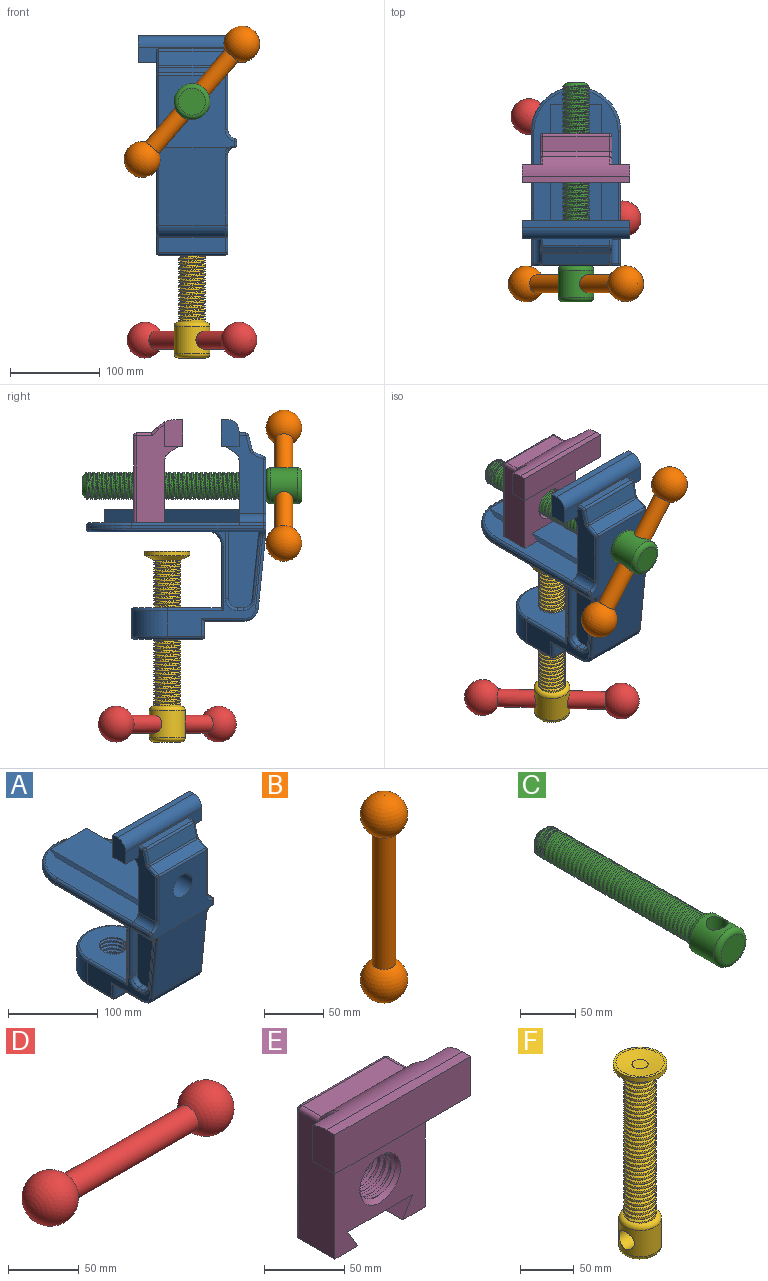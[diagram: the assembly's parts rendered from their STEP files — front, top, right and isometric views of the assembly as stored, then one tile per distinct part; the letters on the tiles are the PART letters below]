
ASSEMBLY  parts=6 mates=5
PART A: 123 faces, bbox 121.3x205.7x246.3 mm
  f0: cylinder r=15mm len=35mm, axis (0,0,1), area 1354.5mm2, adj f2,f4,f120,f121,f122
  f1: plane 117x106.29mm, normal (1,0,0), area 2063.5mm2, adj f8,f26,f77,f86,f87,f88,f89,f90
  f2: plane 98.33x75.33mm, normal (0,0,1), area 5812mm2, adj f0,f7,f103,f105,f107,f121,f122
  f3: plane 94.79x81.43mm, normal (0,-1,0), area 5458.1mm2, adj f27,f36,f57,f59,f60,f64,f65,f67
  f4: plane 75.45x74.02mm, normal (0,0,-1), area 4288.3mm2, adj f0,f90,f92,f93,f94
  f5: plane 74x44.99mm, normal (0,0,-1), area 3328.9mm2, adj f6,f84,f88,f97
  f6: plane 74x17mm, normal (0,-1,0), area 1258mm2, adj f5,f89,f93,f96
  f7: plane 74x70mm, normal (0,1,0), area 5180mm2, adj f2,f76,f102,f106
  f8: plane 193.33x95.05mm, normal (0,0,-1), area 12981.5mm2, adj f1,f25,f28,f29,f31,f32,f34,f35
  f9: plane 167x94mm, normal (0,0,1), area 8749.9mm2, adj f13,f21,f22,f23,f73,f74,f75
  f10: plane 147x4mm, normal (1,0,0), area 588mm2, adj f11,f65,f68,f75
  f11: cylinder r=50mm len=100mm, axis (0,0,-1), area 628.3mm2, adj f10,f12,f70,f74
  f12: plane 147x4mm, normal (-1,0,0), area 588mm2, adj f11,f71,f72,f73
  f13: plane 100x72.47mm, normal (0,1,0), area 4179.3mm2, adj f9,f14,f15,f16,f17,f22,f23,f24
  f14: plane 87x42mm, normal (-1,0,0), area 2053mm2, adj f13,f16,f37,f42,f43,f44,f47,f52
  f15: plane 87x42mm, normal (1,0,0), area 2053mm2, adj f13,f17,f37,f42,f43,f44,f45,f49
  f16: cylinder r=10mm len=27mm, axis (0,-1,0), area 361.2mm2, adj f13,f14,f66,f67
  f17: cylinder r=10mm len=27mm, axis (0,1,0), area 361.2mm2, adj f13,f15,f60,f61
  f18: plane 74x7.66mm, normal (0,0,1), area 566.7mm2, adj f42,f45,f47,f48
  f19: plane 74x12.11mm, normal (0,-0.45,0.89), area 1001.7mm2, adj f53,f54,f58,f59
  f20: plane 74x16.39mm, normal (0,-0.97,0.24), area 1250.1mm2, adj f48,f49,f52,f53
  f21: plane 57.32x15mm, normal (0,1,0), area 729.9mm2, adj f9,f22,f23,f24
  f22: plane 150x15mm, normal (-0.87,0,-0.5), area 2598.1mm2, adj f9,f13,f21,f24
  f23: plane 150x15mm, normal (0.87,0,-0.5), area 2598.1mm2, adj f9,f13,f21,f24
  f24: plane 150x57.32mm, normal (0,0,1), area 8598.1mm2, adj f13,f21,f22,f23
  f25: plane 117x106.29mm, normal (-1,0,0), area 2063.5mm2, adj f8,f26,f78,f94,f96,f97,f98,f99
  f26: cylinder r=40mm len=80mm, axis (0,0,1), area 3644.2mm2, adj f1,f25,f92,f105
  f27: plane 86.49x80.33mm, normal (0,-1,-0.1), area 6446.7mm2, adj f3,f84,f85,f86,f99,f100
  f28: plane 75x7mm, normal (0,-1,0), area 525mm2, adj f8,f31,f82,f114
  f29: plane 76x9.58mm, normal (0,1,0.1), area 540.1mm2, adj f8,f31,f79,f118,f119
  f30: plane 7x6.41mm, normal (0,0,1), area 44.9mm2, adj f31,f79,f82,f116
  f31: plane 85x33.96mm, normal (1,0,0), area 2487mm2, adj f8,f28,f29,f30,f79,f82
  f32: plane 75x7mm, normal (0,-1,0), area 525mm2, adj f8,f35,f81,f108
  f33: plane 7x6.41mm, normal (0,0,1), area 44.9mm2, adj f35,f80,f81,f110
  f34: plane 76x9.58mm, normal (0,1,0.1), area 540.1mm2, adj f8,f35,f80,f112,f113
  f35: plane 85x33.96mm, normal (-1,0,0), area 2487mm2, adj f8,f32,f33,f34,f80,f81
  f36: cylinder r=15mm len=30mm, axis (0,-1,0), area 2827.4mm2, adj f3,f13
  f37: plane 120x20mm, normal (0,0,-1), area 1200mm2, adj f14,f15,f38,f40,f41,f42,f43
  f38: plane 30x20mm, normal (-1,0,0), area 563.7mm2, adj f37,f39,f41,f42,f83
  f39: plane 120x7mm, normal (0,0,1), area 840mm2, adj f38,f40,f41,f83
  f40: plane 30x20mm, normal (1,0,0), area 563.7mm2, adj f37,f39,f41,f42,f83
  f41: plane 120x30mm, normal (0,1,0), area 3600mm2, adj f37,f38,f39,f40
  f42: plane 120x17mm, normal (0,-1,0), area 843.9mm2, adj f14,f15,f18,f37,f38,f40,f45,f47
  f43: plane 80x10.55mm, normal (0,0.55,-0.83), area 1014.1mm2, adj f14,f15,f37,f44
  f44: cylinder r=10mm len=80mm, axis (1,0,0), area 786.2mm2, adj f13,f14,f15,f43
  f45: cylinder r=3mm len=7.66mm, axis (0,-1,0), area 36.1mm2, adj f15,f18,f42,f46
  f46: sphere r=3mm, area 11.9mm2, adj f45,f48,f49
  f47: cylinder r=3mm len=7.66mm, axis (0,1,0), area 36.1mm2, adj f14,f18,f42,f50
  f48: cylinder r=3mm len=74mm, axis (1,0,0), area 294.3mm2, adj f18,f20,f46,f50
  f49: cylinder r=3mm len=17.12mm, axis (0,-0.24,-0.97), area 79.6mm2, adj f15,f20,f46,f51
  f50: sphere r=3mm, area 12.4mm2, adj f47,f48,f52
  f51: torus R=6mm, axis (1,0,0), area 16.6mm2, adj f15,f49,f53,f54
  f52: cylinder r=3mm len=17.12mm, axis (0,-0.24,-0.97), area 79.6mm2, adj f14,f20,f50,f55
  f53: cylinder r=3mm len=74mm, axis (1,0,0), area 191.4mm2, adj f19,f20,f51,f55
  f54: cylinder r=3mm len=13.45mm, axis (0,0.89,0.45), area 63.8mm2, adj f15,f19,f51,f56
  f55: torus R=6mm, axis (1,0,0), area 16.6mm2, adj f14,f52,f53,f58
  f56: sphere r=3mm, area 7.1mm2, adj f54,f57,f59
  f57: cylinder r=3mm len=60.65mm, axis (0,0,1), area 285.8mm2, adj f3,f15,f56,f60
  f58: cylinder r=3mm len=13.45mm, axis (0,0.89,0.45), area 63.8mm2, adj f14,f19,f55,f62
  f59: cylinder r=3mm len=74mm, axis (-1,0,0), area 245.8mm2, adj f3,f19,f56,f62
  f60: torus R=13mm, axis (0,1,0), area 69.9mm2, adj f3,f17,f57,f63
  f61: cylinder r=3mm len=27mm, axis (0,1,0), area 113.1mm2, adj f13,f17,f63,f75
  f62: sphere r=3mm, area 7.1mm2, adj f58,f59,f64
  f63: sphere r=3mm, area 12.1mm2, adj f60,f61,f65,f75
  f64: cylinder r=3mm len=60.65mm, axis (0,0,-1), area 285.8mm2, adj f3,f14,f62,f67
  f65: cylinder r=3mm len=6.71mm, axis (0,0,1), area 27.3mm2, adj f3,f10,f63,f68,f75,f85
  f66: cylinder r=3mm len=27mm, axis (0,-1,0), area 113.1mm2, adj f13,f16,f69,f73
  f67: torus R=13mm, axis (0,1,0), area 69.9mm2, adj f3,f16,f64,f69
  f68: cylinder r=3mm len=149.36mm, axis (0,1,0), area 698.6mm2, adj f8,f10,f65,f70,f77,f85
  f69: sphere r=3mm, area 12.1mm2, adj f66,f67,f71,f73
  f70: torus R=47mm, axis (0,0,1), area 724.1mm2, adj f8,f11,f68,f72
  f71: cylinder r=3mm len=6.71mm, axis (0,0,-1), area 27.3mm2, adj f3,f12,f69,f72,f73,f100
  f72: cylinder r=3mm len=149.36mm, axis (0,-1,0), area 698.6mm2, adj f8,f12,f70,f71,f78,f100
  f73: cylinder r=3mm len=147.35mm, axis (0,1,0), area 570.3mm2, adj f9,f12,f13,f66,f69,f71,f74
  f74: torus R=47mm, axis (0,0,1), area 724.1mm2, adj f9,f11,f73,f75
  f75: cylinder r=3mm len=147.35mm, axis (0,1,0), area 570.3mm2, adj f9,f10,f13,f61,f63,f65,f74
  f76: cylinder r=15mm len=74mm, axis (-1,0,0), area 1743.6mm2, adj f7,f8,f101,f104
  f77: cylinder r=7mm len=7mm, axis (0,-1,0), area 22.1mm2, adj f1,f68,f85,f119
  f78: cylinder r=7mm len=7mm, axis (0,-1,0), area 22.1mm2, adj f25,f72,f100,f113
  f79: cylinder r=10mm len=9.95mm, axis (1,0,0), area 103mm2, adj f29,f30,f31,f117
  f80: cylinder r=10mm len=9.95mm, axis (-1,0,0), area 103mm2, adj f33,f34,f35,f111
  f81: cylinder r=10mm len=10mm, axis (1,0,0), area 110mm2, adj f32,f33,f35,f109
  f82: cylinder r=10mm len=10mm, axis (-1,0,0), area 110mm2, adj f28,f30,f31,f115
  f83: cylinder r=13mm len=120mm, axis (1,0,0), area 2450.4mm2, adj f38,f39,f40,f42
  f84: cylinder r=15mm len=74mm, axis (-1,0,0), area 1633mm2, adj f5,f27,f87,f98
  f85: bspline ~12.3x10mm, area 57.4mm2, adj f3,f27,f65,f68,f77,f86
  f86: cylinder r=3mm len=79.49mm, axis (0,0.1,-1), area 375.1mm2, adj f1,f27,f85,f87
  f87: torus R=12mm, axis (1,0,0), area 96.4mm2, adj f1,f84,f86,f88
  f88: cylinder r=3mm len=47.99mm, axis (0,-1,0), area 219.1mm2, adj f1,f5,f87,f89
  f89: cylinder r=3mm len=20mm, axis (0,0,1), area 87.2mm2, adj f1,f6,f88,f91
  f90: cylinder r=3mm len=38.44mm, axis (0,-1,0), area 181.1mm2, adj f1,f4,f91,f92
  f91: sphere r=3mm, area 14.1mm2, adj f89,f90,f93
  f92: torus R=37mm, axis (0,0,-1), area 576mm2, adj f4,f26,f90,f94
  f93: cylinder r=3mm len=74mm, axis (1,0,0), area 348.7mm2, adj f4,f6,f91,f95
  f94: cylinder r=3mm len=38.44mm, axis (0,-1,0), area 181.1mm2, adj f4,f25,f92,f95
  f95: sphere r=3mm, area 14.1mm2, adj f93,f94,f96
  f96: cylinder r=3mm len=20mm, axis (0,0,1), area 87.2mm2, adj f6,f25,f95,f97
  f97: cylinder r=3mm len=47.99mm, axis (0,-1,0), area 219.1mm2, adj f5,f25,f96,f98
  f98: torus R=12mm, axis (-1,0,0), area 96.4mm2, adj f25,f84,f97,f99
  f99: cylinder r=3mm len=79.49mm, axis (0,-0.1,1), area 375.1mm2, adj f25,f27,f98,f100
  f100: bspline ~12.3x10mm, area 57.4mm2, adj f3,f27,f71,f72,f78,f99
  f101: torus R=18mm, axis (1,0,0), area 96.2mm2, adj f1,f8,f76,f102
  f102: cylinder r=3mm len=73mm, axis (0,0,-1), area 336.9mm2, adj f1,f7,f101,f103
  f103: cylinder r=3mm len=63mm, axis (0,-1,0), area 289.8mm2, adj f1,f2,f102,f105
  f104: torus R=18mm, axis (-1,0,0), area 96.2mm2, adj f8,f25,f76,f106
  f105: torus R=37mm, axis (0,0,1), area 576mm2, adj f2,f26,f103,f107
  f106: cylinder r=3mm len=73mm, axis (0,0,-1), area 336.9mm2, adj f7,f25,f104,f107
  f107: cylinder r=3mm len=63mm, axis (0,-1,0), area 289.8mm2, adj f2,f25,f105,f106
  f108: cylinder r=3mm len=75mm, axis (0,0,1), area 353.4mm2, adj f8,f25,f32,f109
  f109: torus R=13mm, axis (-1,0,0), area 82.1mm2, adj f25,f81,f108,f110
  f110: cylinder r=3mm len=6.41mm, axis (0,1,0), area 30.2mm2, adj f25,f33,f109,f111
  f111: torus R=13mm, axis (-1,0,0), area 76.9mm2, adj f25,f80,f110,f112
  f112: cylinder r=3mm len=69.59mm, axis (0,0.1,-1), area 328.2mm2, adj f25,f34,f111,f113
  f113: bspline ~10.3x10mm, area 44.3mm2, adj f8,f34,f78,f112
  f114: cylinder r=3mm len=75mm, axis (0,0,-1), area 353.4mm2, adj f1,f8,f28,f115
  f115: torus R=13mm, axis (1,0,0), area 82.1mm2, adj f1,f82,f114,f116
  f116: cylinder r=3mm len=6.41mm, axis (0,-1,0), area 30.2mm2, adj f1,f30,f115,f117
  f117: torus R=13mm, axis (1,0,0), area 76.9mm2, adj f1,f79,f116,f118
  f118: cylinder r=3mm len=69.59mm, axis (0,-0.1,1), area 328.2mm2, adj f1,f29,f117,f119
  f119: bspline ~11.74x10mm, area 44.3mm2, adj f8,f29,f77,f118
  f120: plane 3x2.38mm, normal (-0.4,0.92,0), area 3.9mm2, adj f0,f121,f122
  f121: bspline ~40.13x36.5mm, area 1960.7mm2, adj f0,f2,f120,f122
  f122: bspline ~40.13x35.96mm, area 1894.8mm2, adj f0,f2,f120,f121
PART B: 3 faces, bbox 40x40x210 mm
  f0: sphere r=20mm, area 4689.8mm2, adj f1
  f1: cylinder r=10mm len=135.36mm, axis (0,0,-1), area 8504.9mm2, adj f0,f2
  f2: sphere r=20mm, area 4689.8mm2, adj f1
PART C: 11 faces, bbox 43.3x245x43.3 mm
  f0: cylinder r=15mm len=200mm, axis (0,-1,0), area 7941mm2, adj f6,f7,f8,f9,f10
  f1: plane 20x20mm, normal (0,1,0), area 314.2mm2, adj f7
  f2: plane 30x30mm, normal (0,-1,0), area 706.9mm2, adj f5
  f3: cylinder r=10mm len=40mm, axis (0,0,1), area 2347.9mm2, adj f4
  f4: cylinder r=20mm len=40mm, axis (0,-1,0), area 3119.7mm2, adj f3,f5,f6
  f5: torus R=15mm, axis (0,-1,0), area 897.3mm2, adj f2,f4
  f6: torus R=15mm, axis (0,-1,0), area 897.3mm2, adj f0,f4
  f7: cone r=15mm half-angle=45deg, axis (0,-1,0), area 466.7mm2, adj f0,f1,f9,f10
  f8: plane 3x2.38mm, normal (-0.4,0,-0.92), area 3.9mm2, adj f0,f9,f10
  f9: bspline ~203.17x34.64mm, area 9792.7mm2, adj f0,f7,f8,f10
  f10: bspline ~203.17x34.64mm, area 9466.6mm2, adj f0,f7,f8,f9
PART D: 3 faces, bbox 195x40x40 mm
  f0: cylinder r=10mm len=120.36mm, axis (-1,0,0), area 7562.4mm2, adj f1,f2
  f1: sphere r=20mm, area 4689.8mm2, adj f0
  f2: sphere r=20mm, area 4689.8mm2, adj f0
PART E: 38 faces, bbox 120.7x55.7x115.7 mm
  f0: plane 27.93x23.66mm, normal (0,1,0), area 547.6mm2, adj f6,f17,f18,f24,f27
  f1: plane 80x69.65mm, normal (0,-1,0), area 3824.1mm2, adj f4,f5,f6,f9,f10,f11,f12,f13
  f2: cylinder r=15mm len=30mm, axis (0,-1,0), area 1053.4mm2, adj f3,f13,f15,f16
  f3: cone r=15mm half-angle=45deg, axis (0,1,0), area 363mm2, adj f2,f7,f14,f15
  f4: plane 35x20mm, normal (0,0,-1), area 698.1mm2, adj f1,f5,f7,f11,f32
  f5: plane 108.94x47mm, normal (-1,0,0), area 3273.7mm2, adj f1,f4,f17,f22,f25,f26,f32,f35
  f6: plane 108.94x47mm, normal (1,0,0), area 3273.7mm2, adj f0,f1,f9,f17,f25,f26,f27,f28
  f7: plane 97x74mm, normal (0,1,0), area 5430.2mm2, adj f3,f4,f9,f10,f11,f12,f29,f32
  f8: plane 74x17mm, normal (0,0,1), area 1258mm2, adj f23,f30,f33,f35
  f9: plane 35x20mm, normal (0,0,-1), area 698.1mm2, adj f1,f6,f7,f10,f29
  f10: plane 35x15mm, normal (-0.87,0,0.5), area 606.2mm2, adj f1,f7,f9,f12
  f11: plane 35x15mm, normal (0.87,0,0.5), area 606.2mm2, adj f1,f4,f7,f12
  f12: plane 57.32x35mm, normal (0,0,-1), area 2006.2mm2, adj f1,f7,f10,f11
  f13: cone r=15mm half-angle=45deg, axis (0,-1,0), area 338.6mm2, adj f1,f2,f15,f16
  f14: plane 2.42x1.89mm, normal (-0.4,0,0.92), area 0.9mm2, adj f3,f15,f16
  f15: bspline ~40.13x35.96mm, area 1798.1mm2, adj f2,f3,f13,f14,f16
  f16: bspline ~40.13x35.96mm, area 1812.1mm2, adj f2,f13,f14,f15
  f17: plane 120x20mm, normal (0,0,-1), area 1200mm2, adj f0,f5,f6,f18,f20,f21,f22,f25
  f18: plane 30x20mm, normal (1,0,0), area 588.8mm2, adj f0,f17,f19,f21,f24
  f19: plane 120x7.43mm, normal (0,0,1), area 891.8mm2, adj f18,f20,f21,f24
  f20: plane 30x20mm, normal (-1,0,0), area 588.8mm2, adj f17,f19,f21,f22,f24
  f21: plane 120x30mm, normal (0,-1,0), area 3600mm2, adj f17,f18,f19,f20
  f22: plane 27.93x23.66mm, normal (0,1,0), area 547.6mm2, adj f5,f17,f20,f24,f37
  f23: plane 74x6.11mm, normal (0,0.71,0.71), area 639.7mm2, adj f8,f24,f28,f36
  f24: cylinder r=30.34mm len=120mm, axis (-1,0,0), area 2359.6mm2, adj f0,f18,f19,f20,f22,f23,f27,f37
  f25: plane 80x10.55mm, normal (0,-0.55,-0.83), area 1014.1mm2, adj f5,f6,f17,f26
  f26: cylinder r=10mm len=80mm, axis (-1,0,0), area 786.2mm2, adj f1,f5,f6,f25
  f27: torus R=27.34mm, axis (-1,0,0), area 46mm2, adj f0,f6,f24,f28
  f28: cylinder r=3mm len=9.11mm, axis (0,-0.71,0.71), area 43.7mm2, adj f6,f23,f27,f30
  f29: cylinder r=3mm len=97mm, axis (0,0,1), area 457.1mm2, adj f6,f7,f9,f31
  f30: cylinder r=3mm len=18.24mm, axis (0,-1,0), area 83mm2, adj f6,f8,f28,f31
  f31: sphere r=3mm, area 14.1mm2, adj f29,f30,f33
  f32: cylinder r=3mm len=97mm, axis (0,0,-1), area 457.1mm2, adj f4,f5,f7,f34
  f33: cylinder r=3mm len=74mm, axis (1,0,0), area 348.7mm2, adj f7,f8,f31,f34
  f34: sphere r=3mm, area 14.1mm2, adj f32,f33,f35
  f35: cylinder r=3mm len=18.24mm, axis (0,1,0), area 83mm2, adj f5,f8,f34,f36
  f36: cylinder r=3mm len=9.11mm, axis (0,-0.71,0.71), area 43.7mm2, adj f5,f23,f35,f37
  f37: torus R=27.34mm, axis (-1,0,0), area 46mm2, adj f5,f22,f24,f36
PART F: 16 faces, bbox 50x50x213 mm
  f0: cylinder r=15mm len=163mm, axis (0,0,-1), area 2855.5mm2, adj f7,f8,f12,f14,f15
  f1: plane 30x30mm, normal (0,0,-1), area 706.9mm2, adj f6
  f2: cylinder r=10mm len=40mm, axis (1,0,0), area 2513.3mm2, adj f3
  f3: cylinder r=20mm len=40mm, axis (0,0,-1), area 3119.7mm2, adj f2,f6,f7
  f4: cylinder r=25mm len=50mm, axis (0,0,-1), area 785.4mm2, adj f5,f8
  f5: plane 50x50mm, normal (0,0,1), area 373.1mm2, adj f4,f10
  f6: torus R=15mm, axis (0,0,-1), area 897.3mm2, adj f1,f3
  f7: torus R=15mm, axis (0,0,-1), area 897.3mm2, adj f0,f3
  f8: cone r=25mm half-angle=63.4deg, axis (0,0,1), area 1405mm2, adj f0,f4,f11
  f9: plane 15x15mm, normal (0,0,1), area 176.7mm2, adj f10
  f10: cone r=7.5mm half-angle=82.4deg, axis (0,0,1), area 1426.2mm2, adj f5,f9
  f11: bspline ~30.2x27.99mm, area 84.8mm2, adj f8,f13,f15
  f12: plane 3x2.56mm, normal (0.17,-0.98,0), area 3.9mm2, adj f0,f14,f15
  f13: plane 3x1.87mm, normal (0.72,-0.69,0), area 3.9mm2, adj f11,f14,f15
  f14: bspline ~164.5x30.44mm, area 6738.4mm2, adj f0,f12,f13,f15
  f15: bspline ~164.5x30.44mm, area 6417.2mm2, adj f0,f11,f12,f13,f14
PLACE A t=(2.33,56.06,21.75)mm fixed
PLACE B rot(axis=(0,-1,0),139.3deg) t=(52.92,61.06,115.48)mm
PLACE C rot(axis=(0,1,0),40.7deg) t=(-29.63,61.06,38.1)mm
PLACE D rot(axis=(0,0,-1),47.4deg) t=(39.67,39.49,50.05)mm
PLACE E t=(2.33,47.99,21.75)mm
PLACE F rot(axis=(0,0,-1),47.4deg) t=(31.21,48.69,50.05)mm
MATE revolute C.f0 <-> A.f36  axis (0,-1,0) through (8.38,-90.51,73)mm
MATE fastened B.f1 <-> C.f3  axis (0.65,0,0.76) through (8.38,-110.51,73)mm
MATE slider E.f1 <-> A.f21  axis (0,-1,0) through (-15.95,22.23,39.25)mm
MATE fastened D.f0 <-> F.f2  axis (-0.68,0.74,0) through (8.38,19.49,-192.95)mm
MATE cylindrical F.f3 <-> A.f0  axis (0,0,1) through (8.38,19.49,-9.95)mm
